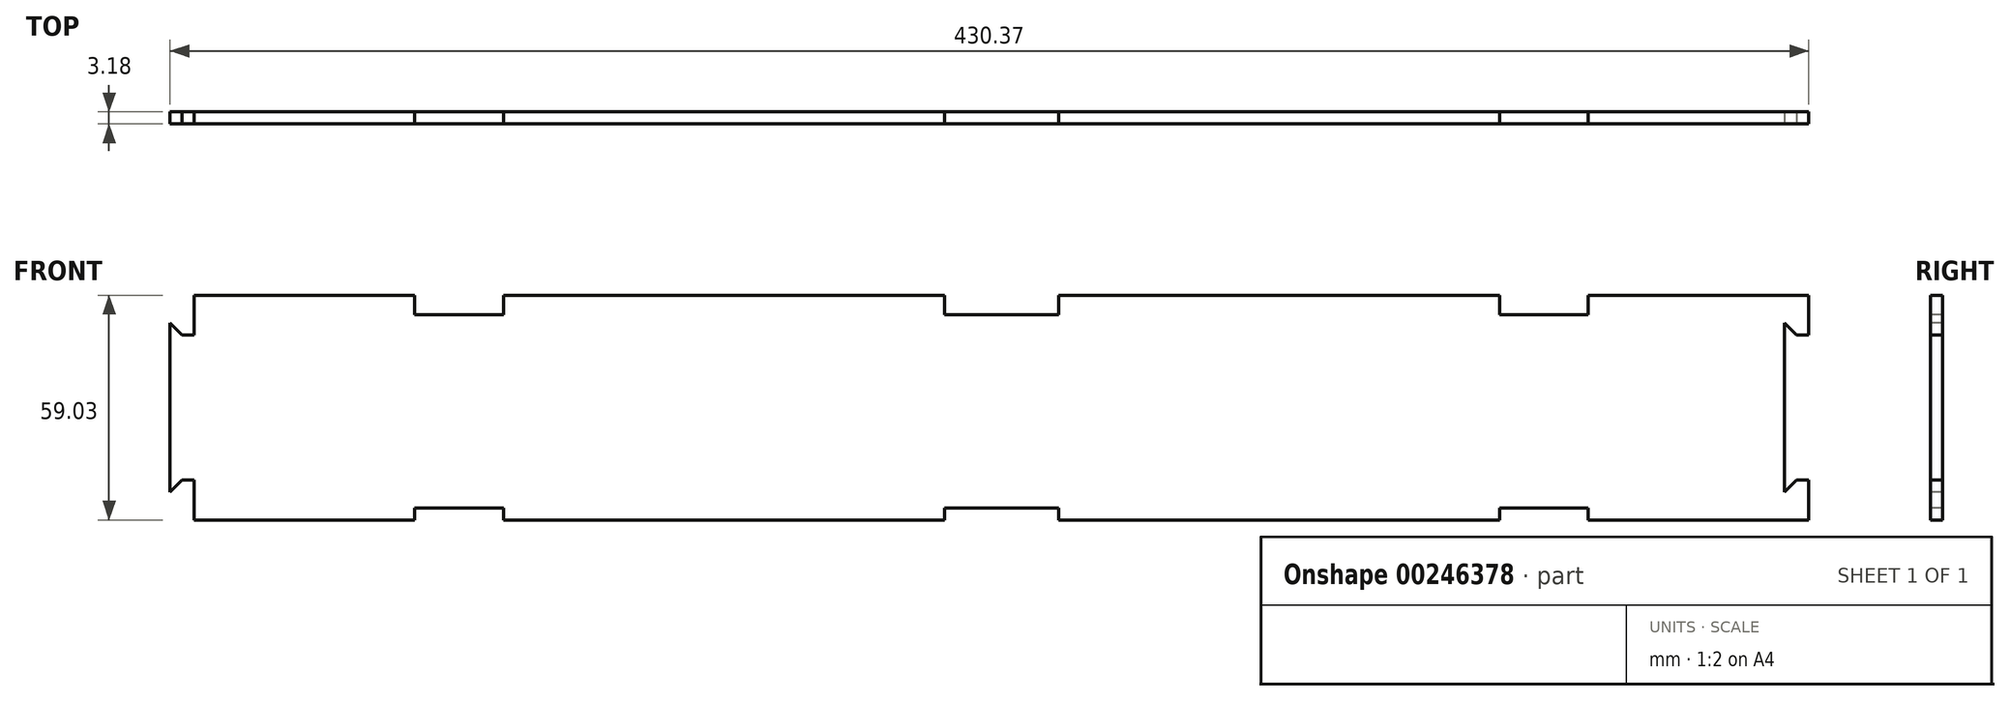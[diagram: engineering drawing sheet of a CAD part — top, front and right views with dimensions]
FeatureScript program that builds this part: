
annotation { "Feature Type Name" : "Feature", "Feature Type Description" : "" }
export const myFeature = defineFeature(function(context is Context, id is Id, definition is map)
    precondition{}
    {
        {
            var Q0;
            Q0=qCreatedBy(makeId("Front.planeOp"),FACE);
            var sketch = newSketch(context, id + "F0", { "sketchPlane" : qUnion([Q0])});
            skLineSegment(sketch, "E0.bottom", {"start": v(0, 0) * mm, "end": v(424.02, 0) * mm});
            skLineSegment(sketch, "E0.top", {"start": v(0, 50.8) * mm, "end": v(424.02, 50.8) * mm});
            skLineSegment(sketch, "E0.left", {"start": v(0, 0) * mm, "end": v(0, 50.8) * mm});
            skLineSegment(sketch, "E0.right", {"start": v(424.02, 0) * mm, "end": v(424.02, 50.8) * mm});
            skSolve(sketch);
        }
        {
            var Q0;
            Q0=makeQuery(id+"F0.imprint","IMPRINT",FACE,{"disambiguationData":[TD([[makeQuery(id+"F0.imprint","IMPRINT",EDGE,{"derivedFrom":sQuery(id+"F0.wireOp",EDGE,"E0.bottom")}),1.0]])]});
            extrude(context, id + "F1", {"entities" : qUnion([Q0]), "depth" : 3.17 * mm});
        }
        {
            var Q0;
            Q0=makeQuery(id+"F1.opExtrude","CAP_FACE",FACE,{"disambiguationData":[OSD([sQuery(id+"F0.wireOp",EDGE,"E0.bottom"),sQuery(id+"F0.wireOp",EDGE,"E0.top"),sQuery(id+"F0.wireOp",EDGE,"E0.left"),sQuery(id+"F0.wireOp",EDGE,"E0.right")])],"isStart":false});
            var sketch = newSketch(context, id + "F2", { "sketchPlane" : qUnion([Q0])});
            skLineSegment(sketch, "E1.bottom", {"start": v(0, 50.8) * mm, "end": v(57.92, 50.8) * mm});
            skLineSegment(sketch, "E1.top", {"start": v(0, 55.88) * mm, "end": v(57.92, 55.88) * mm});
            skLineSegment(sketch, "E1.left", {"start": v(0, 50.8) * mm, "end": v(0, 55.88) * mm});
            skLineSegment(sketch, "E1.right", {"start": v(57.92, 50.8) * mm, "end": v(57.92, 55.88) * mm});
            skLineSegment(sketch, "E2.bottom", {"start": v(81.2, 50.8) * mm, "end": v(197.05, 50.8) * mm});
            skLineSegment(sketch, "E2.top", {"start": v(81.2, 55.88) * mm, "end": v(197.05, 55.88) * mm});
            skLineSegment(sketch, "E2.left", {"start": v(81.2, 50.8) * mm, "end": v(81.2, 55.88) * mm});
            skLineSegment(sketch, "E2.right", {"start": v(197.05, 50.8) * mm, "end": v(197.05, 55.88) * mm});
            skLineSegment(sketch, "E3.bottom", {"start": v(226.97, 50.8) * mm, "end": v(342.82, 50.8) * mm});
            skLineSegment(sketch, "E3.top", {"start": v(226.97, 55.88) * mm, "end": v(342.82, 55.88) * mm});
            skLineSegment(sketch, "E3.left", {"start": v(226.97, 50.8) * mm, "end": v(226.97, 55.88) * mm});
            skLineSegment(sketch, "E3.right", {"start": v(342.82, 50.8) * mm, "end": v(342.82, 55.88) * mm});
            skLineSegment(sketch, "E4.bottom", {"start": v(366.1, 50.8) * mm, "end": v(424.02, 50.8) * mm});
            skLineSegment(sketch, "E4.top", {"start": v(366.1, 55.88) * mm, "end": v(424.02, 55.88) * mm});
            skLineSegment(sketch, "E4.left", {"start": v(366.1, 50.8) * mm, "end": v(366.1, 55.88) * mm});
            skLineSegment(sketch, "E4.right", {"start": v(424.02, 50.8) * mm, "end": v(424.02, 55.88) * mm});
            skLineSegment(sketch, "E5.bottom", {"start": v(0, 0) * mm, "end": v(57.92, 0) * mm});
            skLineSegment(sketch, "E5.top", {"start": v(0, -3.15) * mm, "end": v(57.92, -3.15) * mm});
            skLineSegment(sketch, "E5.left", {"start": v(0, 0) * mm, "end": v(0, -3.15) * mm});
            skLineSegment(sketch, "E5.right", {"start": v(57.92, 0) * mm, "end": v(57.92, -3.15) * mm});
            skLineSegment(sketch, "E6.bottom", {"start": v(81.2, 0) * mm, "end": v(197.05, 0) * mm});
            skLineSegment(sketch, "E6.top", {"start": v(81.2, -3.15) * mm, "end": v(197.05, -3.15) * mm});
            skLineSegment(sketch, "E6.left", {"start": v(81.2, 0) * mm, "end": v(81.2, -3.15) * mm});
            skLineSegment(sketch, "E6.right", {"start": v(197.05, 0) * mm, "end": v(197.05, -3.15) * mm});
            skLineSegment(sketch, "E7.bottom", {"start": v(226.97, 0) * mm, "end": v(342.82, 0) * mm});
            skLineSegment(sketch, "E7.top", {"start": v(226.97, -3.15) * mm, "end": v(342.82, -3.15) * mm});
            skLineSegment(sketch, "E7.left", {"start": v(226.97, 0) * mm, "end": v(226.97, -3.15) * mm});
            skLineSegment(sketch, "E7.right", {"start": v(342.82, 0) * mm, "end": v(342.82, -3.15) * mm});
            skLineSegment(sketch, "E8.bottom", {"start": v(424.02, 0) * mm, "end": v(366.1, 0) * mm});
            skLineSegment(sketch, "E8.top", {"start": v(424.02, -3.15) * mm, "end": v(366.1, -3.15) * mm});
            skLineSegment(sketch, "E8.left", {"start": v(424.02, 0) * mm, "end": v(424.02, -3.15) * mm});
            skLineSegment(sketch, "E8.right", {"start": v(366.1, 0) * mm, "end": v(366.1, -3.15) * mm});
            skSolve(sketch);
        }
        {
            var Q0;
            Q0 = qSketchRegion(id + "F2", true);
            extrude(context, id + "F3", {"entities" : qUnion([Q0]), "operationType" : NewBodyOperationType.ADD, "oppositeDirection" : true, "depth" : 3.17 * mm});
        }
        {
            var Q0;
            Q0=makeQuery(id+"F3.boolean.opBoolean","MERGE",FACE,{"derivedFrom":[makeQuery(id+"F1.opExtrude","CAP_FACE",FACE,{"disambiguationData":[OSD([sQuery(id+"F0.wireOp",EDGE,"E0.bottom"),sQuery(id+"F0.wireOp",EDGE,"E0.top"),sQuery(id+"F0.wireOp",EDGE,"E0.left"),sQuery(id+"F0.wireOp",EDGE,"E0.right")])],"isStart":false}),makeQuery(id+"F3.opExtrude","CAP_FACE",FACE,{"disambiguationData":[OSD([sQuery(id+"F2.wireOp",EDGE,"E1.bottom"),sQuery(id+"F2.wireOp",EDGE,"E1.top"),sQuery(id+"F2.wireOp",EDGE,"E1.left"),sQuery(id+"F2.wireOp",EDGE,"E1.right")])],"isStart":true}),makeQuery(id+"F3.opExtrude","CAP_FACE",FACE,{"disambiguationData":[OSD([sQuery(id+"F2.wireOp",EDGE,"E2.bottom"),sQuery(id+"F2.wireOp",EDGE,"E2.top"),sQuery(id+"F2.wireOp",EDGE,"E2.left"),sQuery(id+"F2.wireOp",EDGE,"E2.right")])],"isStart":true}),makeQuery(id+"F3.opExtrude","CAP_FACE",FACE,{"disambiguationData":[OSD([sQuery(id+"F2.wireOp",EDGE,"E3.bottom"),sQuery(id+"F2.wireOp",EDGE,"E3.top"),sQuery(id+"F2.wireOp",EDGE,"E3.left"),sQuery(id+"F2.wireOp",EDGE,"E3.right")])],"isStart":true}),makeQuery(id+"F3.opExtrude","CAP_FACE",FACE,{"disambiguationData":[OSD([sQuery(id+"F2.wireOp",EDGE,"E4.bottom"),sQuery(id+"F2.wireOp",EDGE,"E4.top"),sQuery(id+"F2.wireOp",EDGE,"E4.left"),sQuery(id+"F2.wireOp",EDGE,"E4.right")])],"isStart":true}),makeQuery(id+"F3.opExtrude","CAP_FACE",FACE,{"disambiguationData":[OSD([sQuery(id+"F2.wireOp",EDGE,"E5.bottom"),sQuery(id+"F2.wireOp",EDGE,"E5.top"),sQuery(id+"F2.wireOp",EDGE,"E5.left"),sQuery(id+"F2.wireOp",EDGE,"E5.right")])],"isStart":true}),makeQuery(id+"F3.opExtrude","CAP_FACE",FACE,{"disambiguationData":[OSD([sQuery(id+"F2.wireOp",EDGE,"E6.bottom"),sQuery(id+"F2.wireOp",EDGE,"E6.top"),sQuery(id+"F2.wireOp",EDGE,"E6.left"),sQuery(id+"F2.wireOp",EDGE,"E6.right")])],"isStart":true}),makeQuery(id+"F3.opExtrude","CAP_FACE",FACE,{"disambiguationData":[OSD([sQuery(id+"F2.wireOp",EDGE,"E7.bottom"),sQuery(id+"F2.wireOp",EDGE,"E7.top"),sQuery(id+"F2.wireOp",EDGE,"E7.left"),sQuery(id+"F2.wireOp",EDGE,"E7.right")])],"isStart":true}),makeQuery(id+"F3.opExtrude","CAP_FACE",FACE,{"disambiguationData":[OSD([sQuery(id+"F2.wireOp",EDGE,"E8.bottom"),sQuery(id+"F2.wireOp",EDGE,"E8.top"),sQuery(id+"F2.wireOp",EDGE,"E8.left"),sQuery(id+"F2.wireOp",EDGE,"E8.right")])],"isStart":true})]});
            var sketch = newSketch(context, id + "F4", { "sketchPlane" : qUnion([Q0])});
            skLineSegment(sketch, "E9", {"start": v(0, 45.42) * mm, "end": v(-3.18, 45.42) * mm});
            skLineSegment(sketch, "E10", {"start": v(-3.18, 45.42) * mm, "end": v(-6.35, 48.6) * mm});
            skLineSegment(sketch, "E11", {"start": v(-6.35, 48.6) * mm, "end": v(-6.35, 4.14) * mm});
            skLineSegment(sketch, "E12", {"start": v(-6.35, 4.14) * mm, "end": v(-3.18, 7.32) * mm});
            skLineSegment(sketch, "E13", {"start": v(-3.18, 7.32) * mm, "end": v(0, 7.32) * mm});
            skLineSegment(sketch, "E14", {"start": v(424.02, 45.42) * mm, "end": v(420.84, 45.42) * mm});
            skLineSegment(sketch, "E15", {"start": v(420.84, 45.42) * mm, "end": v(417.67, 48.6) * mm});
            skLineSegment(sketch, "E16", {"start": v(417.67, 48.6) * mm, "end": v(417.67, 4.14) * mm});
            skLineSegment(sketch, "E17", {"start": v(417.67, 4.14) * mm, "end": v(420.84, 7.32) * mm});
            skLineSegment(sketch, "E18", {"start": v(420.84, 7.32) * mm, "end": v(424.02, 7.32) * mm});
            skPoint(sketch, "E19", {"position": v(0, 26.37) * mm});
            skPoint(sketch, "E20", {"position": v(-6.35, 26.37) * mm});
            skPoint(sketch, "E21", {"position": v(417.67, 26.37) * mm});
            skPoint(sketch, "E22", {"position": v(424.02, 26.37) * mm});
            skLineSegment(sketch, "E23", {"start": v(0, 45.42) * mm, "end": v(0, 7.32) * mm});
            skSolve(sketch);
        }
        {
            var Q0;
            Q0=makeQuery(id+"F4.imprint","IMPRINT",FACE,{"disambiguationData":[TD([[makeQuery(id+"F4.imprint","IMPRINT",EDGE,{"derivedFrom":sQuery(id+"F4.wireOp",EDGE,"E9")}),1.0]])]});
            extrude(context, id + "F5", {"entities" : qUnion([Q0]), "operationType" : NewBodyOperationType.ADD, "oppositeDirection" : true, "depth" : 3.17 * mm});
        }
        {
            var Q0;
            {var subQ0=sQuery(id+"F4.wireOp",EDGE,"E14");Q0=makeQuery(id+"F4.imprint","IMPRINT",FACE,{"disambiguationData":[TD([[makeQuery(id+"F4.imprint","IMPRINT",EDGE,{"derivedFrom":subQ0}),1.0]])]});}
            extrude(context, id + "F6", {"entities" : qUnion([Q0]), "operationType" : NewBodyOperationType.REMOVE, "endBound" : BoundingType.THROUGH_ALL, "oppositeDirection" : true, "depth" : 25.4 * mm});
        }
    });
